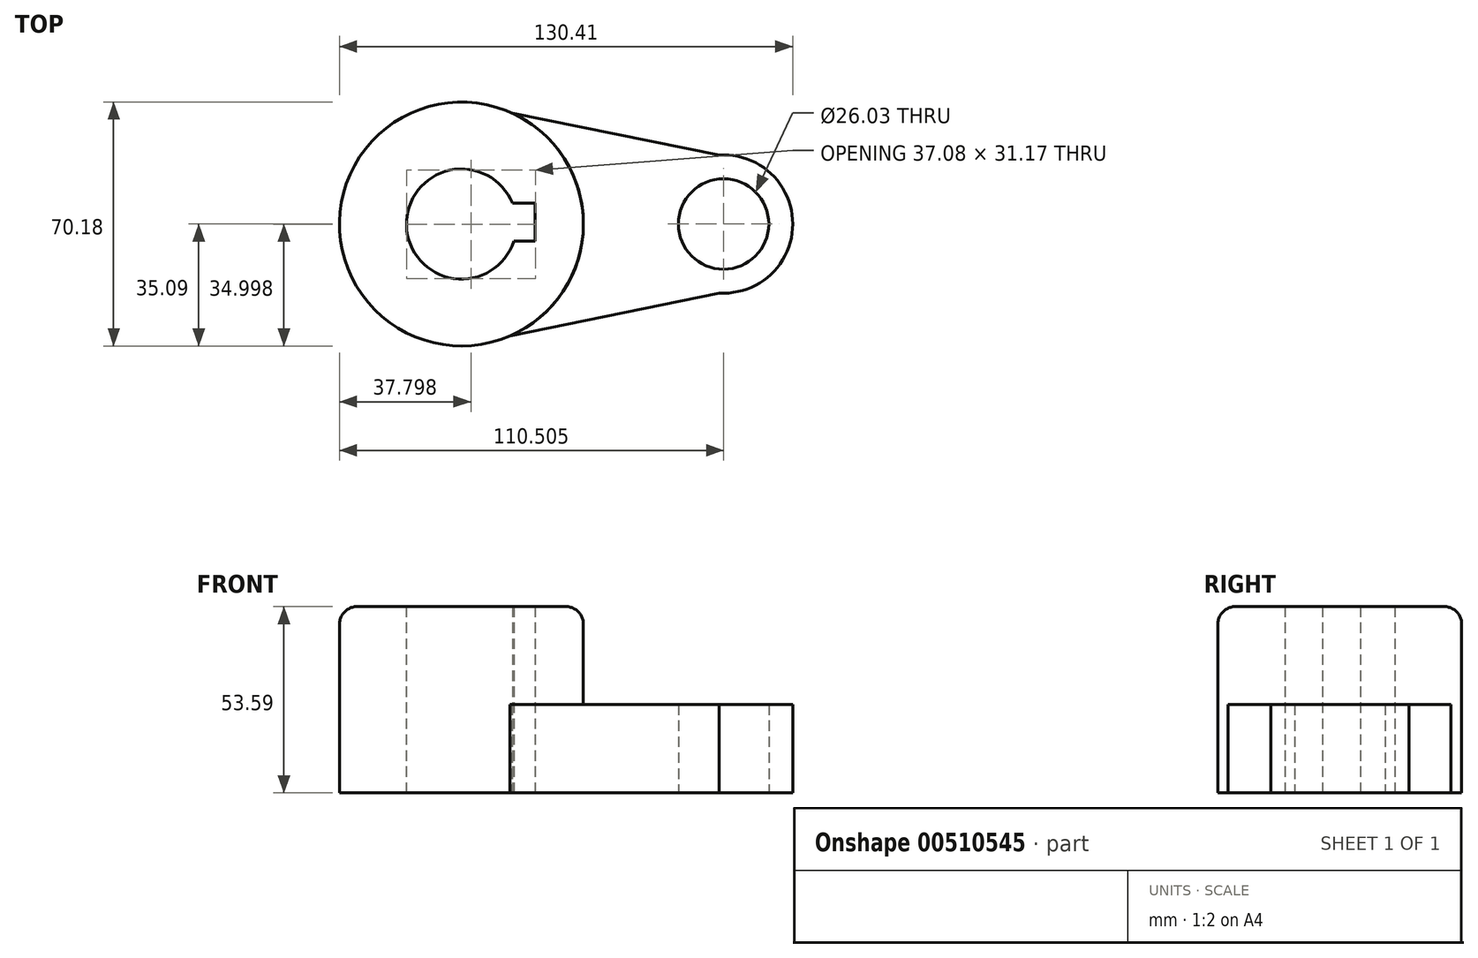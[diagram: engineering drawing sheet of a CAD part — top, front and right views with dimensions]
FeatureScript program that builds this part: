
annotation { "Feature Type Name" : "Feature", "Feature Type Description" : "" }
export const myFeature = defineFeature(function(context is Context, id is Id, definition is map)
    precondition{}
    {
        {
            var Q0;
            Q0=qCreatedBy(makeId("Top.planeOp"),FACE);
            var sketch = newSketch(context, id + "F0", { "sketchPlane" : qUnion([Q0])});
            skCircle(sketch, "E0", {"center": v(0, 0) * mm, "radius": 35.1 * mm});
            skCircle(sketch, "E1", {"center": v(0, 0) * mm, "radius": 15.84 * mm});
            skLineSegment(sketch, "E2", {"start": v(14.67, 5.96) * mm, "end": v(21.25, 5.96) * mm});
            skLineSegment(sketch, "E3", {"start": v(21.25, 5.96) * mm, "end": v(21.25, 0) * mm});
            skLineSegment(sketch, "E4", {"start": v(21.25, 0) * mm, "end": v(21.25, -4.97) * mm});
            skLineSegment(sketch, "E5", {"start": v(21.25, -4.97) * mm, "end": v(15.04, -4.97) * mm});
            skCircle(sketch, "E6", {"center": v(75.42, 0) * mm, "radius": 13.02 * mm});
            skCircle(sketch, "E7", {"center": v(75.42, 0) * mm, "radius": 19.9 * mm});
            skLineSegment(sketch, "E8", {"start": v(14.54, 31.94) * mm, "end": v(74.15, 19.86) * mm});
            skLineSegment(sketch, "E9", {"start": v(74.15, 19.86) * mm, "end": v(74.15, -19.86) * mm});
            skLineSegment(sketch, "E10", {"start": v(74.15, -19.86) * mm, "end": v(13.9, -32.22) * mm});
            skLineSegment(sketch, "E11", {"start": v(13.9, -32.22) * mm, "end": v(14.54, 31.94) * mm});
            skSolve(sketch);
        }
        {
            var Q0;
            {var subQ0=sQuery(id+"F0.wireOp",EDGE,"E11");var subQ4=sQuery(id+"F0.wireOp",EDGE,"E1");var subQ5=makeQuery(id+"F0.imprint","INTERSECT",VERTEX,{"disambiguationData":[OD(0.0)],"derivedFrom":[subQ4,subQ0]});Q0=makeQuery(id+"F0.imprint","IMPRINT",FACE,{"disambiguationData":[TD([[makeQuery(id+"F0.imprint","IMPRINT",EDGE,{"disambiguationData":[TD([[subQ5,-1.0]])],"derivedFrom":subQ4}),-1.0]])]});}
            var Q1;
            {var subQ4=sQuery(id+"F0.wireOp",EDGE,"E2");Q1=makeQuery(id+"F0.imprint","IMPRINT",FACE,{"disambiguationData":[TD([[makeQuery(id+"F0.imprint","IMPRINT",EDGE,{"derivedFrom":subQ4}),1.0]])]});}
            extrude(context, id + "F1", {"entities" : qUnion([Q0, Q1]), "depth" : 53.6 * mm});
        }
        {
            var Q0;
            {var subQ1=sQuery(id+"F0.wireOp",EDGE,"E8");Q0=makeQuery(id+"F0.imprint","IMPRINT",FACE,{"disambiguationData":[TD([[makeQuery(id+"F0.imprint","IMPRINT",EDGE,{"derivedFrom":subQ1}),-1.0]])]});}
            var Q1;
            {var subQ0=sQuery(id+"F0.wireOp",EDGE,"E9");var subQ1=sQuery(id+"F0.wireOp",EDGE,"E6");var subQ2=makeQuery(id+"F0.imprint","INTERSECT",VERTEX,{"disambiguationData":[OD(0.0)],"derivedFrom":[subQ1,subQ0]});Q1=makeQuery(id+"F0.imprint","IMPRINT",FACE,{"disambiguationData":[TD([[makeQuery(id+"F0.imprint","IMPRINT",EDGE,{"disambiguationData":[TD([[subQ2,1.0]])],"derivedFrom":subQ1}),-1.0]])]});}
            var Q2;
            {var subQ0=sQuery(id+"F0.wireOp",EDGE,"E9");var subQ1=sQuery(id+"F0.wireOp",EDGE,"E6");var subQ2=makeQuery(id+"F0.imprint","INTERSECT",VERTEX,{"disambiguationData":[OD(0.0)],"derivedFrom":[subQ1,subQ0]});Q2=makeQuery(id+"F0.imprint","IMPRINT",FACE,{"disambiguationData":[TD([[makeQuery(id+"F0.imprint","IMPRINT",EDGE,{"disambiguationData":[TD([[subQ2,-1.0]])],"derivedFrom":subQ1}),-1.0]])]});}
            extrude(context, id + "F2", {"entities" : qUnion([Q0, Q1, Q2]), "operationType" : NewBodyOperationType.ADD, "depth" : 25.4 * mm});
        }
        {
            var Q0;
            Q0=makeQuery(id+"F1.opExtrude","CAP_EDGE",EDGE,{"disambiguationData":[OSD([sQuery(id+"F0.wireOp",EDGE,"E0")])],"isStart":false});
            fillet(context, id + "F3", {"entities" : qUnion([Q0]), "radius" : 5.08 * mm, "tangentPropagation" : true, "allowEdgeOverflow" : false});
        }
    });
